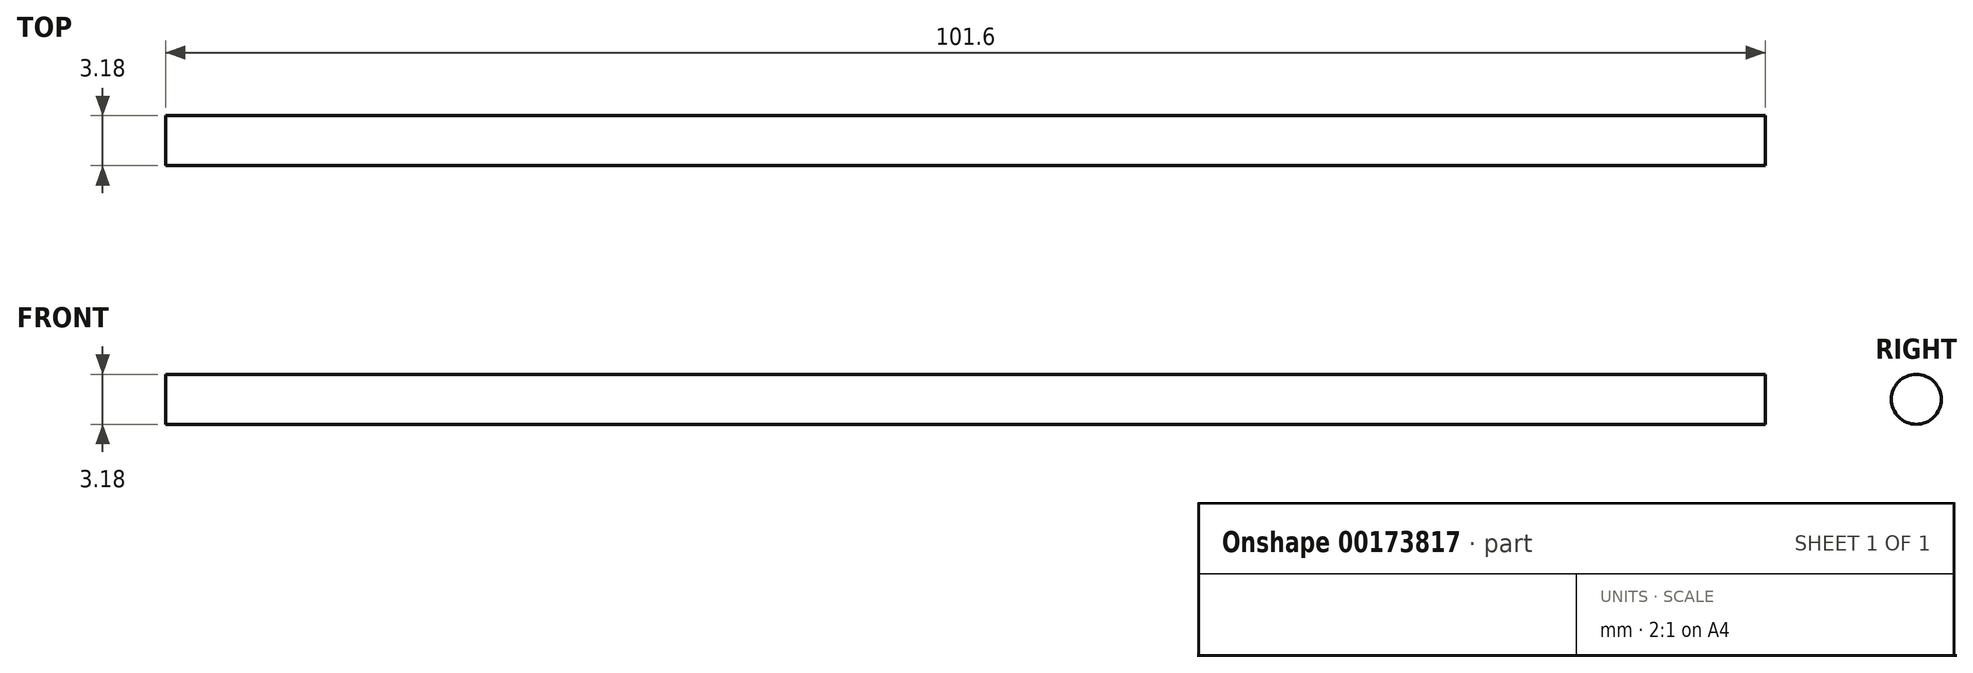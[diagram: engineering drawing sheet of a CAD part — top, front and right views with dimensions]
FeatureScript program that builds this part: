
annotation { "Feature Type Name" : "Feature", "Feature Type Description" : "" }
export const myFeature = defineFeature(function(context is Context, id is Id, definition is map)
    precondition{}
    {
        {
            var Q0;
            Q0=qCreatedBy(makeId("Right.planeOp"),FACE);
            var sketch = newSketch(context, id + "F0", { "sketchPlane" : qUnion([Q0])});
            skCircle(sketch, "E0", {"center": v(0, 0) * mm, "radius": 1.59 * mm});
            skSolve(sketch);
        }
        {
            var Q0;
            Q0 = qSketchRegion(id + "F0", true);
            extrude(context, id + "F1", {"entities" : qUnion([Q0]), "endBound" : BoundingType.SYMMETRIC, "depth" : 101.6 * mm});
        }
    });
